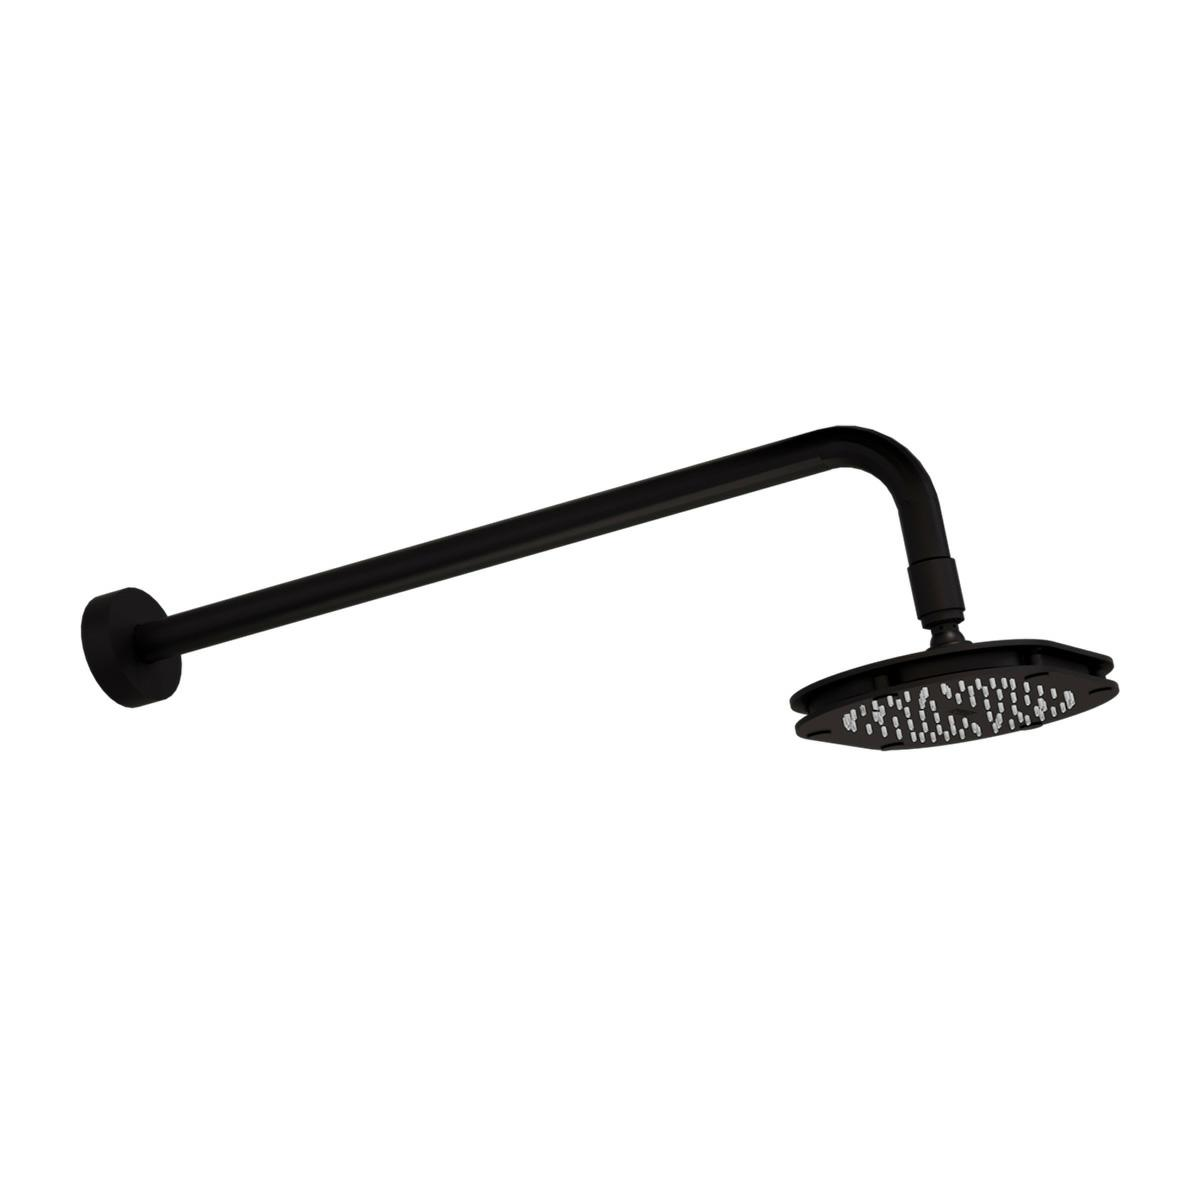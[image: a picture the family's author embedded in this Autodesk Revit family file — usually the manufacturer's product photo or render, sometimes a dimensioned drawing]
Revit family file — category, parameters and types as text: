
# Revit family: H3005-TR035-EB
name_source: partatom
category: Aparatos sanitarios
units: mm (PartAtom-declared; Revit-internal decimal feet)

## family parameters
Activar corte en vistas = No
Anfitrión = Cara
Compartido = Sí
Corte con vacíos al cargar = No
Cota de conector redondo = Usar diámetro
Mantener orientación de anotación = No
Número OmniClass = 23.45.05.14.17
Punto de cálculo de habitación = Sí
Tipo de pieza = Normal
Título OmniClass = Showers

## types (2) — shared parameters
Conexión = ½"-14 NPSM
Elevación por defecto = 0.5 "
Fabricante = HELVEX S.A. DE C.V.
Imagen de tipo = H3005-TR035-EB.jpg
Modelo = H3005-TR035-EB
Presión máxima de trabajo = 85.3 psi
Presión mínima de trabajo = 14.2 psi
Total Diameter = 9.6 "
Total Length = 22.2 "

## per-type parameters (varying)
| type | Comentarios de tipo | Descripción | Material | URL |
| H3005-TR035 | Regadera redonda de plato ancho, multichorro 10"
3 Chorros.
3 Chorros. | Regadera redonda de plato ancho, multichorro 10"
3 Chorros.
3 Chorros. | 192_192_192 |  |
| H3005-TR035-EB | Regadera de chorro fijo con tecnología Aereavex, sistema anticalcáreo. Plato ancho de 5" x 8", Incluye brazo y chapetón. Acabado Ébano. Presión mínima requerida 1.00 kg/cm2. Consumo máximo de agua 1 L/min.
3 Chorros.
3 Chorros. | Regadera de chorro fijo Premier Ébano
3 Chorros.
3 Chorros. | Ébano | https://helvex.com.mx |

## geometry (parser evidence)
native form markers: Sweep x7
no freeform markers — native parametric forms only
